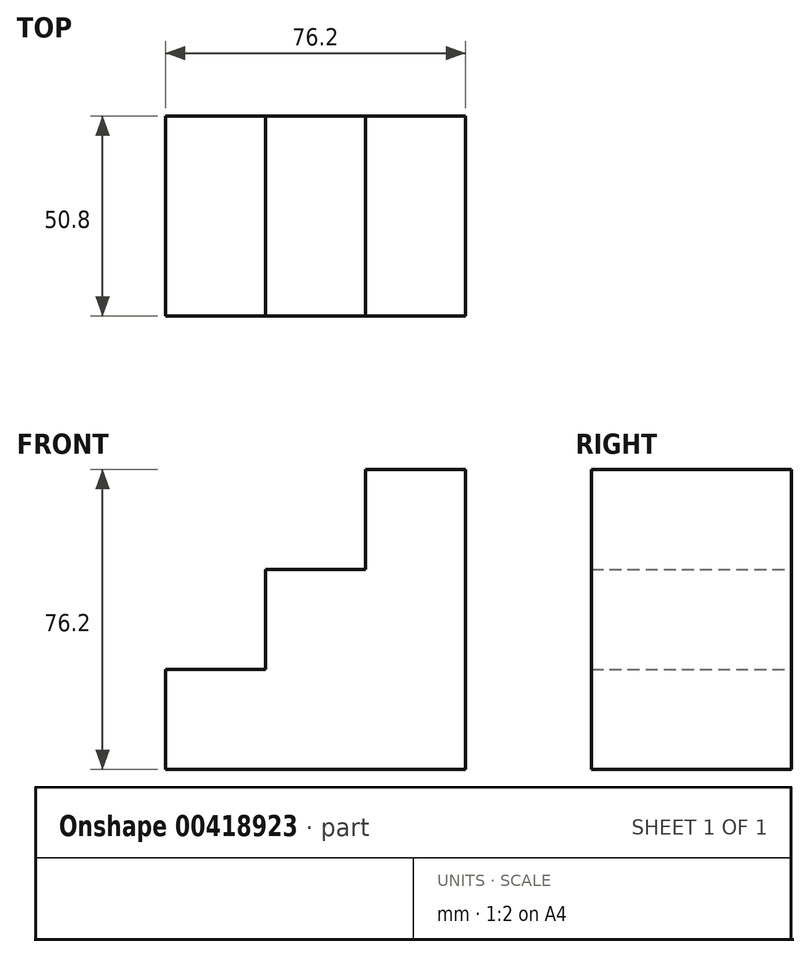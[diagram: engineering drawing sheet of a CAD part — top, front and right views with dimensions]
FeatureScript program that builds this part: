
annotation { "Feature Type Name" : "Feature", "Feature Type Description" : "" }
export const myFeature = defineFeature(function(context is Context, id is Id, definition is map)
    precondition{}
    {
        {
            var Q0;
            Q0=qCreatedBy(makeId("Front.planeOp"),FACE);
            var sketch = newSketch(context, id + "F0", { "sketchPlane" : qUnion([Q0])});
            skLineSegment(sketch, "E0", {"start": v(0, 0) * mm, "end": v(0, 76.2) * mm});
            skLineSegment(sketch, "E1", {"start": v(0, 76.2) * mm, "end": v(-25.4, 76.2) * mm});
            skLineSegment(sketch, "E2", {"start": v(-25.4, 76.2) * mm, "end": v(-25.4, 50.8) * mm});
            skLineSegment(sketch, "E3", {"start": v(-25.4, 50.8) * mm, "end": v(-50.8, 50.8) * mm});
            skLineSegment(sketch, "E4", {"start": v(-50.8, 50.8) * mm, "end": v(-50.8, 25.4) * mm});
            skLineSegment(sketch, "E5", {"start": v(-50.8, 25.4) * mm, "end": v(-76.2, 25.4) * mm});
            skLineSegment(sketch, "E6", {"start": v(-76.2, 25.4) * mm, "end": v(-76.2, 0) * mm});
            skLineSegment(sketch, "E7", {"start": v(-76.2, 0) * mm, "end": v(0, 0) * mm});
            skSolve(sketch);
        }
        {
            var Q0;
            Q0=makeQuery(id+"F0.imprint","IMPRINT",FACE,{"disambiguationData":[TD([[makeQuery(id+"F0.imprint","IMPRINT",EDGE,{"derivedFrom":sQuery(id+"F0.wireOp",EDGE,"E0")}),1.0]])]});
            extrude(context, id + "F1", {"entities" : qUnion([Q0]), "depth" : 50.8 * mm});
        }
    });
